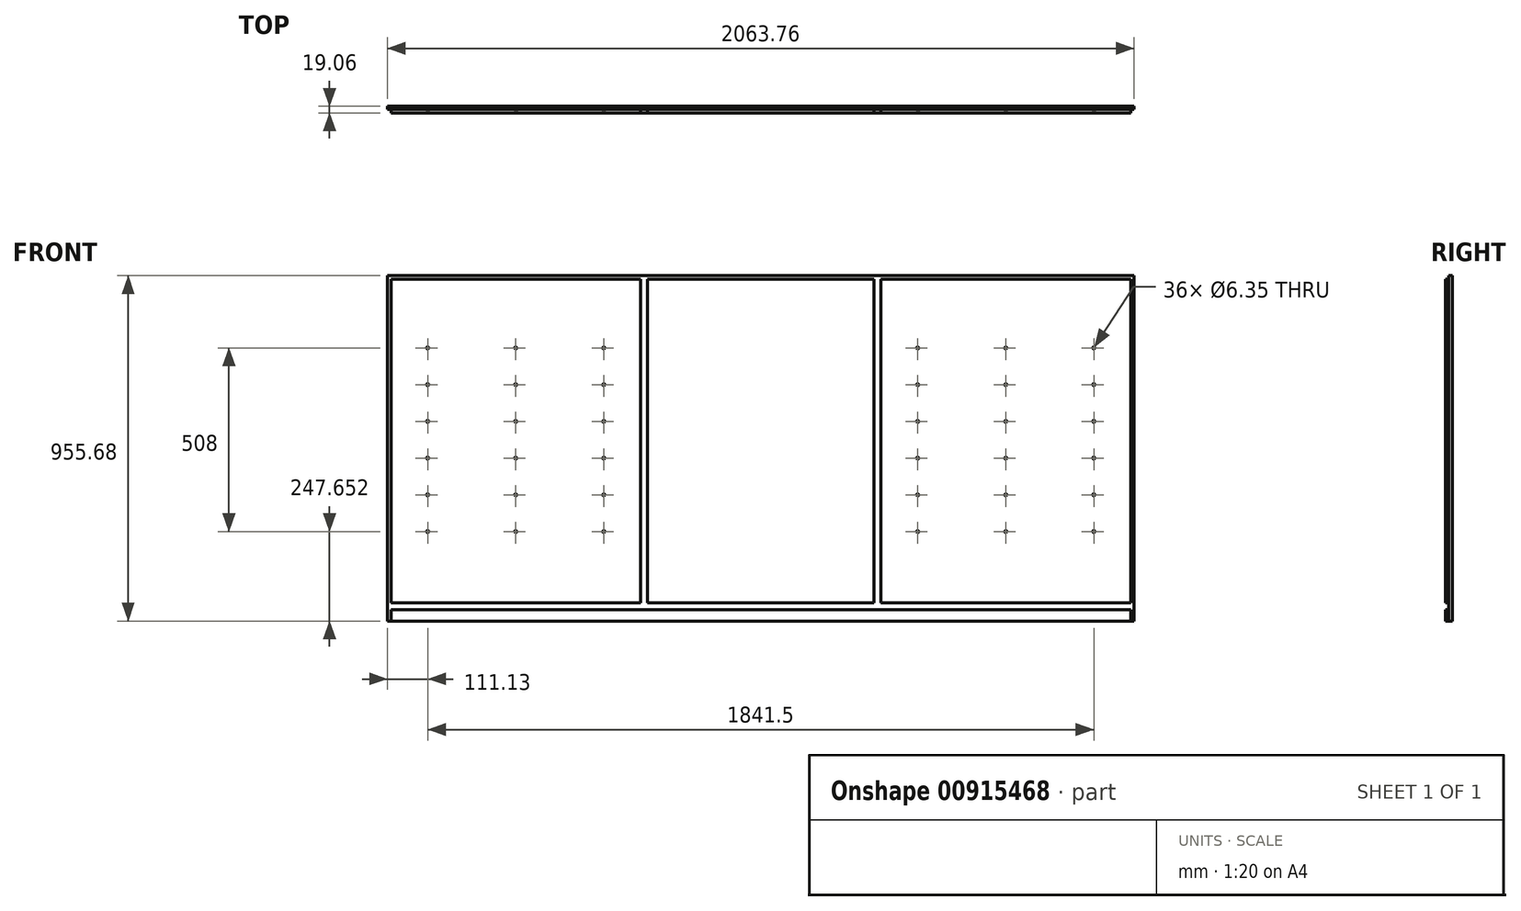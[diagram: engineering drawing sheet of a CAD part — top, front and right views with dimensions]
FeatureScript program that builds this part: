
annotation { "Feature Type Name" : "Feature", "Feature Type Description" : "" }
export const myFeature = defineFeature(function(context is Context, id is Id, definition is map)
    precondition{}
    {
        {
            var Q0;
            Q0=qCreatedBy(makeId("Front.planeOp"),FACE);
            var sketch = newSketch(context, id + "F0", { "sketchPlane" : qUnion([Q0])});
            skLineSegment(sketch, "E0.bottom", {"start": v(1031.88, 477.84) * mm, "end": v(-1031.88, 477.84) * mm});
            skLineSegment(sketch, "E0.top", {"start": v(1031.88, -477.84) * mm, "end": v(-1031.88, -477.84) * mm});
            skLineSegment(sketch, "E0.left", {"start": v(1031.88, 477.84) * mm, "end": v(1031.88, -477.84) * mm});
            skLineSegment(sketch, "E0.right", {"start": v(-1031.88, 477.84) * mm, "end": v(-1031.88, -477.84) * mm});
            skPoint(sketch, "E0.middle", {"position": v(0, 0) * mm});
            skSolve(sketch);
        }
        {
            var Q0;
            Q0=qCreatedBy(makeId("Front.planeOp"),FACE);
            var sketch = newSketch(context, id + "F1", { "sketchPlane" : qUnion([Q0])});
            skLineSegment(sketch, "E1.bottom", {"start": v(-1022.35, 468.31) * mm, "end": v(-332.32, 468.31) * mm});
            skLineSegment(sketch, "E1.top", {"start": v(-1022.35, -427.04) * mm, "end": v(-332.32, -427.04) * mm});
            skLineSegment(sketch, "E1.left", {"start": v(-1022.35, 468.31) * mm, "end": v(-1022.35, -427.04) * mm});
            skLineSegment(sketch, "E1.right", {"start": v(1022.35, 468.31) * mm, "end": v(1022.35, -427.04) * mm});
            skPoint(sketch, "E1.middle", {"position": v(0, 20.64) * mm});
            skLineSegment(sketch, "E2.bottom", {"start": v(-1022.35, -446.09) * mm, "end": v(1022.35, -446.09) * mm});
            skLineSegment(sketch, "E2.top", {"start": v(-1022.35, -477.84) * mm, "end": v(1022.35, -477.84) * mm});
            skLineSegment(sketch, "E2.left", {"start": v(-1022.35, -446.09) * mm, "end": v(-1022.35, -477.84) * mm});
            skLineSegment(sketch, "E2.right", {"start": v(1022.35, -446.09) * mm, "end": v(1022.35, -477.84) * mm});
            skLineSegment(sketch, "E3", {"start": v(313.27, 468.31) * mm, "end": v(313.27, -427.04) * mm});
            skLineSegment(sketch, "E4", {"start": v(332.32, 468.31) * mm, "end": v(332.32, -427.04) * mm});
            skLineSegment(sketch, "E5.trimOffspring", {"start": v(332.32, -427.04) * mm, "end": v(1022.35, -427.04) * mm});
            skLineSegment(sketch, "E6.trimOffspring", {"start": v(332.32, 468.31) * mm, "end": v(1022.35, 468.31) * mm});
            skLineSegment(sketch, "E7", {"start": v(-332.32, 468.31) * mm, "end": v(-332.32, -427.04) * mm});
            skLineSegment(sketch, "E8", {"start": v(-313.27, 468.31) * mm, "end": v(-313.27, -427.04) * mm});
            skLineSegment(sketch, "E9.trimOffspring", {"start": v(-313.27, 468.31) * mm, "end": v(313.27, 468.31) * mm});
            skLineSegment(sketch, "E10.trimOffspring", {"start": v(-313.27, -427.04) * mm, "end": v(313.27, -427.04) * mm});
            skSolve(sketch);
        }
        {
            var Q0;
            Q0 = qSketchRegion(id + "F0", true);
            extrude(context, id + "F2", {"entities" : qUnion([Q0]), "oppositeDirection" : true, "depth" : 9.52 * mm, "offsetDistance" : 25.4 * mm});
        }
        {
            var Q0;
            Q0 = qSketchRegion(id + "F1", true);
            extrude(context, id + "F3", {"entities" : qUnion([Q0]), "operationType" : NewBodyOperationType.ADD, "depth" : 9.52 * mm, "offsetDistance" : 25.4 * mm});
        }
        {
            var Q0;
            Q0=makeQuery(id+"F3.opExtrude","CAP_FACE",FACE,{"disambiguationData":[OSD([sQuery(id+"F1.wireOp",EDGE,"E1.bottom"),sQuery(id+"F1.wireOp",EDGE,"E1.top"),sQuery(id+"F1.wireOp",EDGE,"E1.left"),sQuery(id+"F1.wireOp",EDGE,"E7")])],"isStart":false});
            var sketch = newSketch(context, id + "F4", { "sketchPlane" : qUnion([Q0])});
            skPoint(sketch, "E11", {"position": v(-920.75, 277.81) * mm});
            skPoint(sketch, "E12", {"position": v(920.75, 277.81) * mm});
            skPoint(sketch, "E13.0.1.0", {"position": v(-920.75, 176.21) * mm});
            skPoint(sketch, "E13.0.2.0", {"position": v(-920.75, 74.61) * mm});
            skPoint(sketch, "E13.0.3.0", {"position": v(-920.75, -26.99) * mm});
            skPoint(sketch, "E13.0.4.0", {"position": v(-920.75, -128.59) * mm});
            skPoint(sketch, "E13.0.5.0", {"position": v(-920.75, -230.19) * mm});
            skPoint(sketch, "E13.1.0.0", {"position": v(-677.34, 277.81) * mm});
            skPoint(sketch, "E13.1.1.0", {"position": v(-677.34, 176.21) * mm});
            skPoint(sketch, "E13.1.2.0", {"position": v(-677.34, 74.61) * mm});
            skPoint(sketch, "E13.1.3.0", {"position": v(-677.34, -26.99) * mm});
            skPoint(sketch, "E13.1.4.0", {"position": v(-677.34, -128.59) * mm});
            skPoint(sketch, "E13.1.5.0", {"position": v(-677.34, -230.19) * mm});
            skPoint(sketch, "E13.2.0.0", {"position": v(-433.92, 277.81) * mm});
            skPoint(sketch, "E13.2.1.0", {"position": v(-433.92, 176.21) * mm});
            skPoint(sketch, "E13.2.2.0", {"position": v(-433.92, 74.61) * mm});
            skPoint(sketch, "E13.2.3.0", {"position": v(-433.92, -26.99) * mm});
            skPoint(sketch, "E13.2.4.0", {"position": v(-433.92, -128.59) * mm});
            skPoint(sketch, "E13.2.5.0", {"position": v(-433.92, -230.19) * mm});
            skLineSegment(sketch, "E13.direction1", {"start": v(-920.75, 277.81) * mm, "end": v(-677.34, 277.81) * mm, "construction": true});
            skLineSegment(sketch, "E13.direction2", {"start": v(-920.75, 277.81) * mm, "end": v(-920.75, 176.21) * mm, "construction": true});
            skPoint(sketch, "E14.0.1.0", {"position": v(920.75, 176.21) * mm});
            skPoint(sketch, "E14.0.2.0", {"position": v(920.75, 74.61) * mm});
            skPoint(sketch, "E14.0.3.0", {"position": v(920.75, -26.99) * mm});
            skPoint(sketch, "E14.0.4.0", {"position": v(920.75, -128.59) * mm});
            skPoint(sketch, "E14.0.5.0", {"position": v(920.75, -230.19) * mm});
            skPoint(sketch, "E14.1.0.0", {"position": v(677.34, 277.81) * mm});
            skPoint(sketch, "E14.1.1.0", {"position": v(677.34, 176.21) * mm});
            skPoint(sketch, "E14.1.2.0", {"position": v(677.34, 74.61) * mm});
            skPoint(sketch, "E14.1.3.0", {"position": v(677.34, -26.99) * mm});
            skPoint(sketch, "E14.1.4.0", {"position": v(677.34, -128.59) * mm});
            skPoint(sketch, "E14.1.5.0", {"position": v(677.34, -230.19) * mm});
            skPoint(sketch, "E14.2.0.0", {"position": v(433.92, 277.81) * mm});
            skPoint(sketch, "E14.2.1.0", {"position": v(433.92, 176.21) * mm});
            skPoint(sketch, "E14.2.2.0", {"position": v(433.92, 74.61) * mm});
            skPoint(sketch, "E14.2.3.0", {"position": v(433.92, -26.99) * mm});
            skPoint(sketch, "E14.2.4.0", {"position": v(433.92, -128.59) * mm});
            skPoint(sketch, "E14.2.5.0", {"position": v(433.92, -230.19) * mm});
            skLineSegment(sketch, "E14.direction1", {"start": v(920.75, 277.81) * mm, "end": v(677.34, 277.81) * mm, "construction": true});
            skLineSegment(sketch, "E14.direction2", {"start": v(920.75, 277.81) * mm, "end": v(920.75, 176.21) * mm, "construction": true});
            skSolve(sketch);
        }
        {
            var Q0;
            Q0=sQuery(id+"F4.wireOp",VERTEX,"E13.0.2.0");
            var Q1;
            Q1=sQuery(id+"F4.wireOp",VERTEX,"E13.1.0.0");
            var Q2;
            Q2=sQuery(id+"F4.wireOp",VERTEX,"E13.2.4.0");
            var Q3;
            Q3=sQuery(id+"F4.wireOp",VERTEX,"E13.0.5.0");
            var Q4;
            Q4=sQuery(id+"F4.wireOp",VERTEX,"E13.2.3.0");
            var Q5;
            Q5=sQuery(id+"F4.wireOp",VERTEX,"E13.1.3.0");
            var Q6;
            Q6=sQuery(id+"F4.wireOp",VERTEX,"E13.2.2.0");
            var Q7;
            Q7=sQuery(id+"F4.wireOp",VERTEX,"E11");
            var Q8;
            Q8=sQuery(id+"F4.wireOp",VERTEX,"E13.0.3.0");
            var Q9;
            Q9=sQuery(id+"F4.wireOp",VERTEX,"E13.2.0.0");
            var Q10;
            Q10=sQuery(id+"F4.wireOp",VERTEX,"E13.2.5.0");
            var Q11;
            Q11=sQuery(id+"F4.wireOp",VERTEX,"E13.2.1.0");
            var Q12;
            Q12=sQuery(id+"F4.wireOp",VERTEX,"E13.1.5.0");
            var Q13;
            Q13=sQuery(id+"F4.wireOp",VERTEX,"E13.0.4.0");
            var Q14;
            Q14=sQuery(id+"F4.wireOp",VERTEX,"E13.1.2.0");
            var Q15;
            Q15=sQuery(id+"F4.wireOp",VERTEX,"E13.1.1.0");
            var Q16;
            Q16=sQuery(id+"F4.wireOp",VERTEX,"E13.0.1.0");
            var Q17;
            Q17=sQuery(id+"F4.wireOp",VERTEX,"E13.1.4.0");
            var Q18;
            Q18=sQuery(id+"F4.wireOp",VERTEX,"E14.1.4.0");
            var Q19;
            Q19=sQuery(id+"F4.wireOp",VERTEX,"E14.1.1.0");
            var Q20;
            Q20=sQuery(id+"F4.wireOp",VERTEX,"E14.2.0.0");
            var Q21;
            Q21=sQuery(id+"F4.wireOp",VERTEX,"E12");
            var Q22;
            Q22=sQuery(id+"F4.wireOp",VERTEX,"E14.0.5.0");
            var Q23;
            Q23=sQuery(id+"F4.wireOp",VERTEX,"E14.1.5.0");
            var Q24;
            Q24=sQuery(id+"F4.wireOp",VERTEX,"E14.0.2.0");
            var Q25;
            Q25=sQuery(id+"F4.wireOp",VERTEX,"E14.0.3.0");
            var Q26;
            Q26=sQuery(id+"F4.wireOp",VERTEX,"E14.0.4.0");
            var Q27;
            Q27=sQuery(id+"F4.wireOp",VERTEX,"E14.1.2.0");
            var Q28;
            Q28=sQuery(id+"F4.wireOp",VERTEX,"E14.1.0.0");
            var Q29;
            Q29=sQuery(id+"F4.wireOp",VERTEX,"E14.2.5.0");
            var Q30;
            Q30=sQuery(id+"F4.wireOp",VERTEX,"E14.2.1.0");
            var Q31;
            Q31=sQuery(id+"F4.wireOp",VERTEX,"E14.2.4.0");
            var Q32;
            Q32=sQuery(id+"F4.wireOp",VERTEX,"E14.1.3.0");
            var Q33;
            Q33=sQuery(id+"F4.wireOp",VERTEX,"E14.2.2.0");
            var Q34;
            Q34=sQuery(id+"F4.wireOp",VERTEX,"E14.2.3.0");
            var Q35;
            Q35=sQuery(id+"F4.wireOp",VERTEX,"E14.0.1.0");
            var Q36;
            Q36=makeQuery(id+"F2.opExtrude","SWEPT_BODY",BODY,{"disambiguationData":[OSD([sQuery(id+"F0.wireOp",EDGE,"E0.bottom"),sQuery(id+"F0.wireOp",EDGE,"E0.top"),sQuery(id+"F0.wireOp",EDGE,"E0.left"),sQuery(id+"F0.wireOp",EDGE,"E0.right")])]});
            hole(context, id + "F5", {"style" : HoleStyle.SIMPLE, "endStyle" : HoleEndStyle.BLIND, "holeDiameter" : 6.35 * mm, "majorDiameter" : 6.35 * mm, "holeDepth" : 6.35 * mm, "isTappedThrough" : true, "tappedDepth" : 12.7 * mm, "tapClearance" : 3, "startFromSketch" : true, "locations" : qUnion([Q0, Q1, Q2, Q3, Q4, Q5, Q6, Q7, Q8, Q9, Q10, Q11, Q12, Q13, Q14, Q15, Q16, Q17, Q18, Q19, Q20, Q21, Q22, Q23, Q24, Q25, Q26, Q27, Q28, Q29, Q30, Q31, Q32, Q33, Q34, Q35]), "scope" : qUnion([Q36])});
        }
    });
